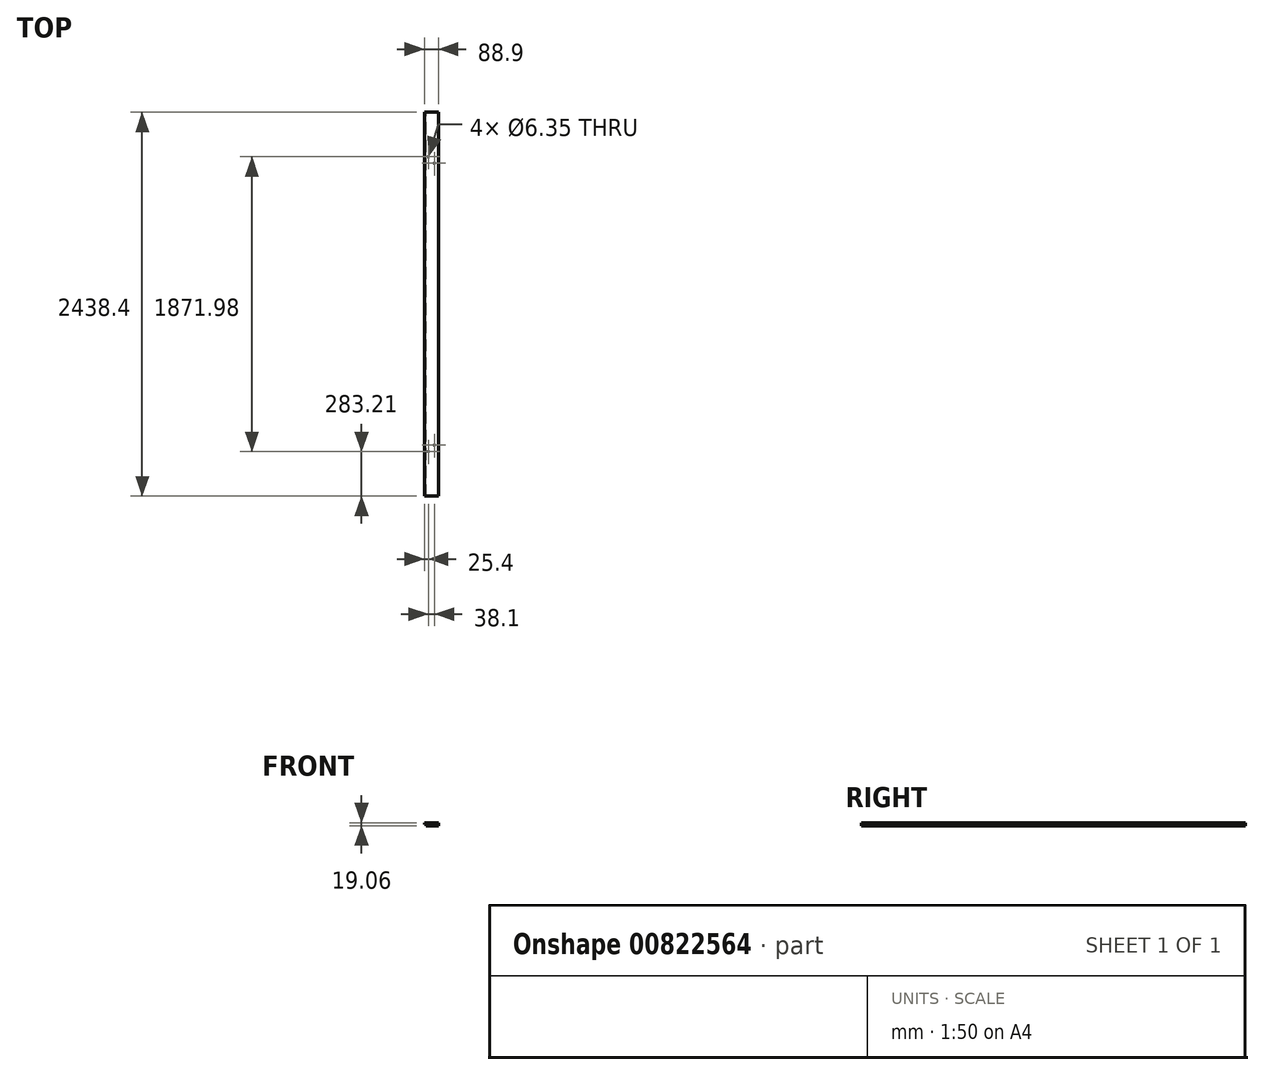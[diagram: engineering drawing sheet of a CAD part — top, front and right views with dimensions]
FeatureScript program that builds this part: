
annotation { "Feature Type Name" : "Feature", "Feature Type Description" : "" }
export const myFeature = defineFeature(function(context is Context, id is Id, definition is map)
    precondition{}
    {
        {
            var Q0;
            Q0=qCreatedBy(makeId("Front.planeOp"),FACE);
            var sketch = newSketch(context, id + "F0", { "sketchPlane" : qUnion([Q0])});
            skLineSegment(sketch, "E0.bottom", {"start": v(-44.45, 9.52) * mm, "end": v(44.45, 9.52) * mm});
            skLineSegment(sketch, "E0.top", {"start": v(-44.45, -9.52) * mm, "end": v(44.45, -9.52) * mm});
            skLineSegment(sketch, "E0.left", {"start": v(-44.45, 9.52) * mm, "end": v(-44.45, -9.52) * mm});
            skLineSegment(sketch, "E0.right", {"start": v(44.45, 9.52) * mm, "end": v(44.45, -9.52) * mm});
            skLineSegment(sketch, "E1", {"start": v(-44.45, -9.53) * mm, "end": v(44.45, 9.53) * mm, "construction": true});
            skSolve(sketch);
        }
        {
            var Q0;
            Q0=makeQuery(id+"F0.imprint","IMPRINT",FACE,{"disambiguationData":[TD([[makeQuery(id+"F0.imprint","IMPRINT",EDGE,{"derivedFrom":sQuery(id+"F0.wireOp",EDGE,"E0.bottom")}),-1.0]])]});
            extrude(context, id + "F1", {"entities" : qUnion([Q0]), "endBound" : BoundingType.SYMMETRIC, "depth" : 2438.4 * mm, "offsetDistance" : 25.4 * mm});
        }
        {
            var Q0;
            Q0=makeQuery(id+"F1.opExtrude","CAP_FACE",FACE,{"disambiguationData":[OSD([sQuery(id+"F0.wireOp",EDGE,"E0.bottom"),sQuery(id+"F0.wireOp",EDGE,"E0.top"),sQuery(id+"F0.wireOp",EDGE,"E0.left"),sQuery(id+"F0.wireOp",EDGE,"E0.right")])],"isStart":false});
            var sketch = newSketch(context, id + "F2", { "sketchPlane" : qUnion([Q0])});
            skLineSegment(sketch, "E2.bottom", {"start": v(-51.1, 0) * mm, "end": v(-34.92, 0) * mm});
            skLineSegment(sketch, "E2.top", {"start": v(-51.1, -19.63) * mm, "end": v(-34.92, -19.63) * mm});
            skLineSegment(sketch, "E2.left", {"start": v(-51.1, 0) * mm, "end": v(-51.1, -19.63) * mm});
            skLineSegment(sketch, "E2.right", {"start": v(-34.92, 0) * mm, "end": v(-34.92, -19.63) * mm});
            skSolve(sketch);
        }
        {
            var Q0;
            Q0 = qSketchRegion(id + "F2", true);
            extrude(context, id + "F3", {"entities" : qUnion([Q0]), "operationType" : NewBodyOperationType.REMOVE, "endBound" : BoundingType.UP_TO_NEXT, "oppositeDirection" : true, "depth" : 25.4 * mm, "offsetDistance" : 25.4 * mm});
        }
        {
            var Q0;
            Q0=makeQuery(id+"F1.opExtrude","SWEPT_FACE",FACE,{"disambiguationData":[OSD([sQuery(id+"F0.wireOp",EDGE,"E0.bottom")])]});
            var sketch = newSketch(context, id + "F4", { "sketchPlane" : qUnion([Q0])});
            skLineSegment(sketch, "E3", {"start": v(0, 0) * mm, "end": v(-88.06, 0) * mm, "construction": true});
            skLineSegment(sketch, "E4", {"start": v(0, -895.35) * mm, "end": v(0, 0) * mm, "construction": true});
            skLineSegment(sketch, "E5.bottom", {"start": v(19.05, -895.35) * mm, "end": v(-19.05, -895.35) * mm, "construction": true});
            skLineSegment(sketch, "E5.top", {"start": v(19.05, -936) * mm, "end": v(-19.05, -936) * mm, "construction": true});
            skLineSegment(sketch, "E5.left", {"start": v(19.05, -936) * mm, "end": v(19.05, -895.35) * mm, "construction": true});
            skLineSegment(sketch, "E5.right", {"start": v(-19.05, -936) * mm, "end": v(-19.05, -895.35) * mm, "construction": true});
            skCircle(sketch, "E6", {"center": v(19.05, -895.35) * mm, "radius": 3.18 * mm});
            skCircle(sketch, "E7", {"center": v(-19.05, -936) * mm, "radius": 3.18 * mm});
            skCircle(sketch, "E8.MirrorC", {"center": v(-19.05, 936) * mm, "radius": 3.18 * mm});
            skCircle(sketch, "E9.MirrorC", {"center": v(19.05, 895.35) * mm, "radius": 3.18 * mm});
            skSolve(sketch);
        }
        {
            var Q0;
            Q0 = qSketchRegion(id + "F4", true);
            extrude(context, id + "F5", {"entities" : qUnion([Q0]), "operationType" : NewBodyOperationType.REMOVE, "endBound" : BoundingType.UP_TO_NEXT, "oppositeDirection" : true, "depth" : 25.4 * mm, "offsetDistance" : 25.4 * mm});
        }
    });
